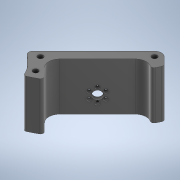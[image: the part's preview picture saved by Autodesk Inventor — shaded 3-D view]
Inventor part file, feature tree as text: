
AUTODESK INVENTOR PART (.ipt)
format: ipt  version: 2020 (Build 240168000, 168)  size: 475,136 bytes
history: native  units: mm
features: sketch x7, extrude x7, chamfer x2, projected_geometry x2, other x1, fillet x1
ambient origin geometry x8: Origin, YZ Plane, XZ Plane, XY Plane, X Axis, Y Axis, Z Axis, Center Point
bodies: Body1 (feature_tree)
feature tree (20):
  other  "Твердое тело1"
  sketch  "Эскиз1"
  extrude  "Выдавливание10"  Depth=3.8mm
  sketch  "Эскиз6"
  extrude  "Выдавливание13"  Depth=6.0mm
  extrude  "Выдавливание14"  Depth=35.0mm TaperAngle=0.0deg
  chamfer  "Фаска3"  Distance=59.0mm
  extrude  "Выдавливание15"  Depth=16.5mm
  fillet  "Сопряжение1"  Radius=10.0mm
  extrude  "Выдавливание16"  Depth=6.4mm
  extrude  "Выдавливание17"  Depth=2.3mm
  sketch  "Эскиз10"
  extrude  "Выдавливание18"  Depth=60.0mm TaperAngle=360.0deg
  chamfer  "Фаска4"  Distance=33.5mm
  sketch  "Эскиз7"
  sketch  "Эскиз8"
  projected_geometry  "Спроецированная петля3"
  sketch  "Эскиз9"
  projected_geometry  "Спроецированная петля4"
  sketch  "Эскиз11"
